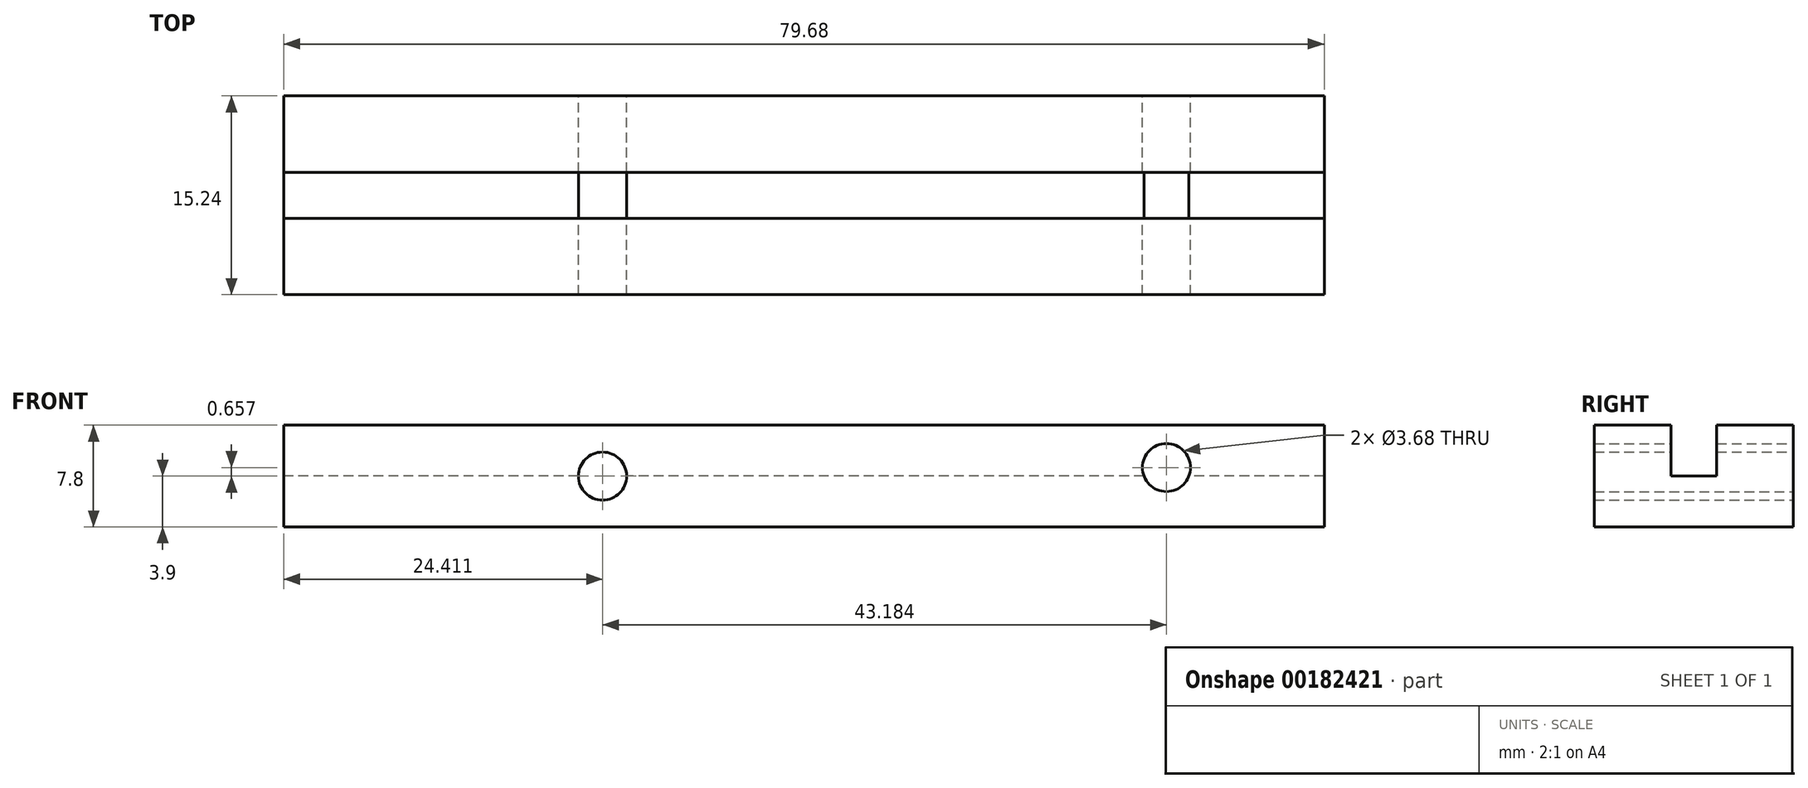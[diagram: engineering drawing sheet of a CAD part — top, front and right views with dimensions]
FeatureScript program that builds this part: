
annotation { "Feature Type Name" : "Feature", "Feature Type Description" : "" }
export const myFeature = defineFeature(function(context is Context, id is Id, definition is map)
    precondition{}
    {
        {
            var Q0;
            Q0=qCreatedBy(makeId("Front.planeOp"),FACE);
            var sketch = newSketch(context, id + "F0", { "sketchPlane" : qUnion([Q0])});
            skLineSegment(sketch, "E0.bottom", {"start": v(39.84, 3.9) * mm, "end": v(-39.84, 3.9) * mm});
            skLineSegment(sketch, "E0.top", {"start": v(39.84, -3.9) * mm, "end": v(-39.84, -3.9) * mm});
            skLineSegment(sketch, "E0.left", {"start": v(39.84, 3.9) * mm, "end": v(39.84, -3.9) * mm});
            skLineSegment(sketch, "E0.right", {"start": v(-39.84, 3.9) * mm, "end": v(-39.84, -3.9) * mm});
            skPoint(sketch, "E0.middle", {"position": v(0, 0) * mm});
            skSolve(sketch);
        }
        {
            var Q0;
            Q0 = qSketchRegion(id + "F0", true);
            extrude(context, id + "F1", {"entities" : qUnion([Q0]), "depth" : 15.24 * mm});
        }
        {
            var Q0;
            Q0=qCreatedBy(makeId("Right.planeOp"),FACE);
            var sketch = newSketch(context, id + "F2", { "sketchPlane" : qUnion([Q0])});
            skLineSegment(sketch, "E1", {"start": v(-15.23, 3.87) * mm, "end": v(0, 3.87) * mm});
            skLineSegment(sketch, "E2.bottom", {"start": v(-5.86, 0) * mm, "end": v(-9.37, 0) * mm});
            skLineSegment(sketch, "E2.top", {"start": v(-5.86, 7.74) * mm, "end": v(-9.37, 7.74) * mm});
            skLineSegment(sketch, "E2.left", {"start": v(-5.86, 0) * mm, "end": v(-5.86, 7.74) * mm});
            skLineSegment(sketch, "E2.right", {"start": v(-9.37, 0) * mm, "end": v(-9.37, 7.74) * mm});
            skPoint(sketch, "E2.middle", {"position": v(-7.62, 3.87) * mm});
            skSolve(sketch);
        }
        {
            var Q0;
            Q0 = qSketchRegion(id + "F2", true);
            extrude(context, id + "F3", {"entities" : qUnion([Q0]), "operationType" : NewBodyOperationType.REMOVE, "endBound" : BoundingType.SYMMETRIC, "depth" : 127 * mm});
        }
        {
            var Q0;
            Q0=makeQuery(id+"F1.opExtrude","CAP_FACE",FACE,{"disambiguationData":[OSD([sQuery(id+"F0.wireOp",EDGE,"E0.bottom"),sQuery(id+"F0.wireOp",EDGE,"E0.top"),sQuery(id+"F0.wireOp",EDGE,"E0.left"),sQuery(id+"F0.wireOp",EDGE,"E0.right")])],"isStart":true});
            var sketch = newSketch(context, id + "F4", { "sketchPlane" : qUnion([Q0])});
            skCircle(sketch, "E3", {"center": v(-27.75, 0.66) * mm, "radius": 1.84 * mm});
            skCircle(sketch, "E4", {"center": v(15.43, 0) * mm, "radius": 1.84 * mm});
            skSolve(sketch);
        }
        {
            var Q0;
            Q0 = qSketchRegion(id + "F4", true);
            extrude(context, id + "F5", {"entities" : qUnion([Q0]), "operationType" : NewBodyOperationType.REMOVE, "oppositeDirection" : true, "depth" : 32.74 * mm});
        }
    });
